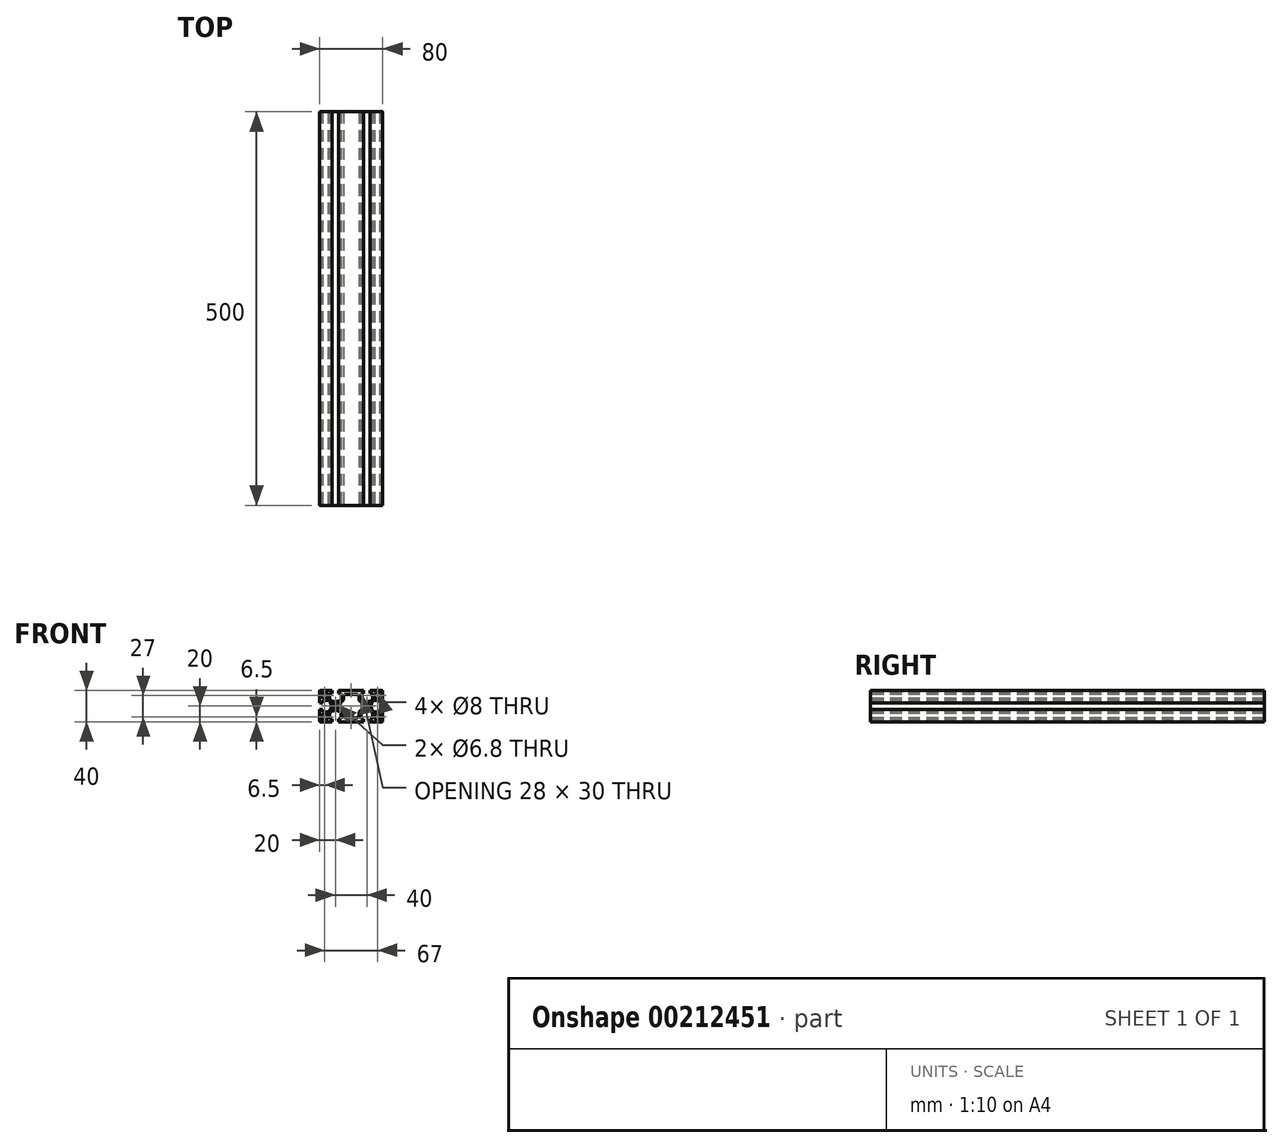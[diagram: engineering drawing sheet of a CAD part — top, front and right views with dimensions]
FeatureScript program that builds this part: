
annotation { "Feature Type Name" : "Feature", "Feature Type Description" : "" }
export const myFeature = defineFeature(function(context is Context, id is Id, definition is map)
    precondition{}
    {
        {
            assignVariable(context, id + "F0", {"name" : "L", "anyValue" : 500});
        }
        {
            var Q0;
            Q0=qCreatedBy(makeId("Front.planeOp"),FACE);
            var sketch = newSketch(context, id + "F1", { "sketchPlane" : qUnion([Q0])});
            skLineSegment(sketch, "E0.bottom", {"start": v(40, 20) * mm, "end": v(-40, 20) * mm});
            skLineSegment(sketch, "E0.top", {"start": v(40, -20) * mm, "end": v(-40, -20) * mm});
            skLineSegment(sketch, "E0.left", {"start": v(40, 20) * mm, "end": v(40, -20) * mm});
            skLineSegment(sketch, "E0.right", {"start": v(-40, 20) * mm, "end": v(-40, -20) * mm});
            skPoint(sketch, "E0.middle", {"position": v(0, 0) * mm});
            skSolve(sketch);
        }
        {
            var Q0;
            Q0=qSketchRegion(id+"F1",true);
            extrude(context, id + "F2", {"entities" : qUnion([Q0]), "endBound" : BoundingType.SYMMETRIC, "depth" : (getVariable(context, 'L')) * mm});
        }
        {
            var Q0;
            Q0=qCreatedBy(makeId("Front.planeOp"),FACE);
            var sketch = newSketch(context, id + "F3", { "sketchPlane" : qUnion([Q0])});
            skLineSegment(sketch, "E1.bottom", {"start": v(33.5, 13.5) * mm, "end": v(-33.5, 13.5) * mm, "construction": true});
            skLineSegment(sketch, "E1.top", {"start": v(33.5, -13.5) * mm, "end": v(-33.5, -13.5) * mm, "construction": true});
            skLineSegment(sketch, "E1.left", {"start": v(33.5, 13.5) * mm, "end": v(33.5, -13.5) * mm, "construction": true});
            skLineSegment(sketch, "E1.right", {"start": v(-33.5, 13.5) * mm, "end": v(-33.5, -13.5) * mm, "construction": true});
            skPoint(sketch, "E1.middle", {"position": v(0, 0) * mm});
            skCircle(sketch, "E2", {"center": v(-33.5, 13.5) * mm, "radius": 4 * mm});
            skCircle(sketch, "E3", {"center": v(-33.5, -13.5) * mm, "radius": 4 * mm});
            skCircle(sketch, "E4", {"center": v(33.5, -13.5) * mm, "radius": 4 * mm});
            skCircle(sketch, "E5", {"center": v(33.5, 13.5) * mm, "radius": 4 * mm});
            skLineSegment(sketch, "E6", {"start": v(-20, 0) * mm, "end": v(20, 0) * mm, "construction": true});
            skCircle(sketch, "E7", {"center": v(-20, 0) * mm, "radius": 3.4 * mm});
            skCircle(sketch, "E8", {"center": v(20, 0) * mm, "radius": 3.4 * mm});
            skSolve(sketch);
        }
        {
            var Q0;
            Q0=qSketchRegion(id+"F3",true);
            extrude(context, id + "F4", {"entities" : qUnion([Q0]), "operationType" : NewBodyOperationType.REMOVE, "endBound" : BoundingType.THROUGH_ALL, "oppositeDirection" : true, "depth" : 25 * mm, "hasSecondDirection" : true, "secondDirectionBound" : SecondDirectionBoundingType.THROUGH_ALL, "secondDirectionOppositeDirection" : false, "secondDirectionDepth" : 25 * mm});
        }
        {
            var Q0;
            Q0=qCreatedBy(makeId("Front.planeOp"),FACE);
            var sketch = newSketch(context, id + "F5", { "sketchPlane" : qUnion([Q0])});
            skLineSegment(sketch, "E9", {"start": v(-24.2, 20) * mm, "end": v(-15.8, 20) * mm});
            skLineSegment(sketch, "E10", {"start": v(-15.8, 20) * mm, "end": v(-15.8, 16) * mm});
            skLineSegment(sketch, "E11", {"start": v(-15.8, 16) * mm, "end": v(-12.75, 16) * mm});
            skLineSegment(sketch, "E12", {"start": v(-12.75, 16) * mm, "end": v(-12.75, 8.86) * mm});
            skLineSegment(sketch, "E13", {"start": v(-24.2, 20) * mm, "end": v(-24.2, 16) * mm});
            skLineSegment(sketch, "E14", {"start": v(-24.2, 16) * mm, "end": v(-27.25, 16) * mm});
            skLineSegment(sketch, "E15", {"start": v(-27.25, 16) * mm, "end": v(-27.25, 8.86) * mm});
            skLineSegment(sketch, "E16", {"start": v(-20, 20) * mm, "end": v(-20, 0) * mm, "construction": true});
            skArc(sketch, "E17", {"start": v(-27.25, 8.86) * mm, "mid": v(-20, 5.5) * mm, "end": v(-12.75, 8.86) * mm});
            skLineSegment(sketch, "E18.1.0", {"start": v(-40, -4.2) * mm, "end": v(-36, -4.2) * mm});
            skLineSegment(sketch, "E18.1.1", {"start": v(-36, -4.2) * mm, "end": v(-36, -7.25) * mm});
            skLineSegment(sketch, "E18.1.2", {"start": v(-36, -7.25) * mm, "end": v(-28.86, -7.25) * mm});
            skArc(sketch, "E18.1.3", {"start": v(-28.86, -7.25) * mm, "mid": v(-25.5, 0) * mm, "end": v(-28.86, 7.25) * mm});
            skLineSegment(sketch, "E18.1.4", {"start": v(-36, 7.25) * mm, "end": v(-28.86, 7.25) * mm});
            skLineSegment(sketch, "E18.1.5", {"start": v(-36, 4.2) * mm, "end": v(-36, 7.25) * mm});
            skLineSegment(sketch, "E18.1.6", {"start": v(-40, 4.2) * mm, "end": v(-36, 4.2) * mm});
            skLineSegment(sketch, "E18.1.7", {"start": v(-40, -4.2) * mm, "end": v(-40, 4.2) * mm});
            skLineSegment(sketch, "E18.2.0", {"start": v(-15.8, -20) * mm, "end": v(-15.8, -16) * mm});
            skLineSegment(sketch, "E18.2.1", {"start": v(-15.8, -16) * mm, "end": v(-12.75, -16) * mm});
            skLineSegment(sketch, "E18.2.2", {"start": v(-12.75, -16) * mm, "end": v(-12.75, -8.86) * mm});
            skArc(sketch, "E18.2.3", {"start": v(-12.75, -8.86) * mm, "mid": v(-20, -5.5) * mm, "end": v(-27.25, -8.86) * mm});
            skLineSegment(sketch, "E18.2.4", {"start": v(-27.25, -16) * mm, "end": v(-27.25, -8.86) * mm});
            skLineSegment(sketch, "E18.2.5", {"start": v(-24.2, -16) * mm, "end": v(-27.25, -16) * mm});
            skLineSegment(sketch, "E18.2.6", {"start": v(-24.2, -20) * mm, "end": v(-24.2, -16) * mm});
            skLineSegment(sketch, "E18.2.7", {"start": v(-15.8, -20) * mm, "end": v(-24.2, -20) * mm});
            skPoint(sketch, "E18.center", {"position": v(-20, 0) * mm});
            skLineSegment(sketch, "E18.anchor1", {"start": v(-20, 0) * mm, "end": v(-24.2, 16) * mm, "construction": true});
            skLineSegment(sketch, "E18.anchor2", {"start": v(-20, 0) * mm, "end": v(-15.8, -16) * mm, "construction": true});
            skLineSegment(sketch, "E19", {"start": v(0, -20) * mm, "end": v(0, 24.43) * mm, "construction": true});
            skArc(sketch, "E20.MirrorCS", {"start": v(12.75, -8.86) * mm, "mid": v(20, -5.5) * mm, "end": v(27.25, -8.86) * mm});
            skLineSegment(sketch, "E21.MirrorCS", {"start": v(40, -4.2) * mm, "end": v(36, -4.2) * mm});
            skLineSegment(sketch, "E22.MirrorCS", {"start": v(12.75, 16) * mm, "end": v(12.75, 8.86) * mm});
            skLineSegment(sketch, "E23.MirrorCS", {"start": v(27.25, -16) * mm, "end": v(27.25, -8.86) * mm});
            skLineSegment(sketch, "E24.MirrorCS", {"start": v(20, 0) * mm, "end": v(15.8, -16) * mm, "construction": true});
            skLineSegment(sketch, "E25.MirrorCS", {"start": v(15.8, -16) * mm, "end": v(12.75, -16) * mm});
            skPoint(sketch, "E26.MirrorP", {"position": v(20, 0) * mm});
            skLineSegment(sketch, "E27.MirrorCS", {"start": v(24.2, -16) * mm, "end": v(27.25, -16) * mm});
            skLineSegment(sketch, "E28.MirrorCS", {"start": v(20, 20) * mm, "end": v(20, 0) * mm, "construction": true});
            skLineSegment(sketch, "E29.MirrorCS", {"start": v(20, 0) * mm, "end": v(24.2, 16) * mm, "construction": true});
            skLineSegment(sketch, "E30.MirrorCS", {"start": v(40, -4.2) * mm, "end": v(40, 4.2) * mm});
            skArc(sketch, "E31.MirrorCS", {"start": v(28.86, -7.25) * mm, "mid": v(25.5, 0) * mm, "end": v(28.86, 7.25) * mm});
            skLineSegment(sketch, "E32.MirrorCS", {"start": v(36, -7.25) * mm, "end": v(28.86, -7.25) * mm});
            skLineSegment(sketch, "E33.MirrorCS", {"start": v(36, -4.2) * mm, "end": v(36, -7.25) * mm});
            skArc(sketch, "E34.MirrorCS", {"start": v(27.25, 8.86) * mm, "mid": v(20, 5.5) * mm, "end": v(12.75, 8.86) * mm});
            skLineSegment(sketch, "E35.MirrorCS", {"start": v(27.25, 16) * mm, "end": v(27.25, 8.86) * mm});
            skLineSegment(sketch, "E36.MirrorCS", {"start": v(15.8, -20) * mm, "end": v(24.2, -20) * mm});
            skLineSegment(sketch, "E37.MirrorCS", {"start": v(24.2, -20) * mm, "end": v(24.2, -16) * mm});
            skLineSegment(sketch, "E38.MirrorCS", {"start": v(24.2, 20) * mm, "end": v(24.2, 16) * mm});
            skLineSegment(sketch, "E39.MirrorCS", {"start": v(15.8, 16) * mm, "end": v(12.75, 16) * mm});
            skLineSegment(sketch, "E40.MirrorCS", {"start": v(15.8, 20) * mm, "end": v(15.8, 16) * mm});
            skLineSegment(sketch, "E41.MirrorCS", {"start": v(24.2, 20) * mm, "end": v(15.8, 20) * mm});
            skLineSegment(sketch, "E42.MirrorCS", {"start": v(15.8, -20) * mm, "end": v(15.8, -16) * mm});
            skLineSegment(sketch, "E43.MirrorCS", {"start": v(12.75, -16) * mm, "end": v(12.75, -8.86) * mm});
            skLineSegment(sketch, "E44.MirrorCS", {"start": v(40, 4.2) * mm, "end": v(36, 4.2) * mm});
            skLineSegment(sketch, "E45.MirrorCS", {"start": v(36, 7.25) * mm, "end": v(28.86, 7.25) * mm});
            skLineSegment(sketch, "E46.MirrorCS", {"start": v(36, 4.2) * mm, "end": v(36, 7.25) * mm});
            skLineSegment(sketch, "E47.MirrorCS", {"start": v(24.2, 16) * mm, "end": v(27.25, 16) * mm});
            skSolve(sketch);
        }
        {
            var Q0;
            Q0=qSketchRegion(id+"F5",true);
            extrude(context, id + "F6", {"entities" : qUnion([Q0]), "operationType" : NewBodyOperationType.REMOVE, "endBound" : BoundingType.THROUGH_ALL, "oppositeDirection" : true, "depth" : 25 * mm, "hasSecondDirection" : true, "secondDirectionBound" : SecondDirectionBoundingType.THROUGH_ALL, "secondDirectionOppositeDirection" : false, "secondDirectionDepth" : 25 * mm});
        }
        {
            var Q0;
            Q0=qCreatedBy(makeId("Front.planeOp"),FACE);
            var sketch = newSketch(context, id + "F7", { "sketchPlane" : qUnion([Q0])});
            skLineSegment(sketch, "E48.bottom", {"start": v(-6.75, 15) * mm, "end": v(6.75, 15) * mm});
            skLineSegment(sketch, "E48.top", {"start": v(-6.75, -15) * mm, "end": v(6.75, -15) * mm});
            skLineSegment(sketch, "E48.left", {"start": v(-9.75, 12) * mm, "end": v(-9.75, 7.85) * mm});
            skLineSegment(sketch, "E48.right", {"start": v(9.75, 12) * mm, "end": v(9.75, 7.85) * mm});
            skLineSegment(sketch, "E49.left", {"start": v(-14, 4.03) * mm, "end": v(-14, -4.03) * mm});
            skLineSegment(sketch, "E49.right", {"start": v(14, 4.03) * mm, "end": v(14, -4.03) * mm});
            skLineSegment(sketch, "E50", {"start": v(0, 15) * mm, "end": v(0, -15) * mm, "construction": true});
            skLineSegment(sketch, "E51", {"start": v(0, 20) * mm, "end": v(0, -26.61) * mm, "construction": true});
            skArc(sketch, "E52.0", {"start": v(-14, 4.03) * mm, "mid": v(-11.65, 5.7) * mm, "end": v(-9.75, 7.85) * mm});
            skLineSegment(sketch, "E53", {"start": v(-20, 0) * mm, "end": v(20, 0) * mm, "construction": true});
            skArc(sketch, "E54.0", {"start": v(-9.75, -7.85) * mm, "mid": v(-11.65, -5.7) * mm, "end": v(-14, -4.03) * mm});
            skArc(sketch, "E55.0", {"start": v(14, 4.03) * mm, "mid": v(11.65, 5.7) * mm, "end": v(9.75, 7.85) * mm});
            skArc(sketch, "E56.0", {"start": v(9.75, -7.85) * mm, "mid": v(11.65, -5.7) * mm, "end": v(14, -4.03) * mm});
            skLineSegment(sketch, "E57.trimOffspring", {"start": v(9.75, -7.85) * mm, "end": v(9.75, -12) * mm});
            skLineSegment(sketch, "E58.trimOffspring", {"start": v(-9.75, -7.85) * mm, "end": v(-9.75, -12) * mm});
            skPoint(sketch, "E59.visualSharp", {"position": v(-9.75, 15) * mm});
            skArc(sketch, "E59.filletArc", {"start": v(-6.75, 15) * mm, "mid": v(-8.87, 14.12) * mm, "end": v(-9.75, 12) * mm});
            skPoint(sketch, "E60.visualSharp", {"position": v(-9.75, -15) * mm});
            skArc(sketch, "E60.filletArc", {"start": v(-9.75, -12) * mm, "mid": v(-8.87, -14.12) * mm, "end": v(-6.75, -15) * mm});
            skPoint(sketch, "E61.visualSharp", {"position": v(9.75, -15) * mm});
            skArc(sketch, "E61.filletArc", {"start": v(6.75, -15) * mm, "mid": v(8.87, -14.12) * mm, "end": v(9.75, -12) * mm});
            skPoint(sketch, "E62.visualSharp", {"position": v(9.75, 15) * mm});
            skArc(sketch, "E62.filletArc", {"start": v(9.75, 12) * mm, "mid": v(8.87, 14.12) * mm, "end": v(6.75, 15) * mm});
            skSolve(sketch);
        }
        {
            var Q0;
            Q0=qSketchRegion(id+"F7",true);
            extrude(context, id + "F8", {"entities" : qUnion([Q0]), "operationType" : NewBodyOperationType.REMOVE, "endBound" : BoundingType.THROUGH_ALL, "oppositeDirection" : true, "depth" : 25 * mm, "hasSecondDirection" : true, "secondDirectionBound" : SecondDirectionBoundingType.THROUGH_ALL, "secondDirectionOppositeDirection" : false, "secondDirectionDepth" : 25 * mm});
        }
        {
            var Q0;
            Q0=makeQuery(id+"F2.opExtrude","SWEPT_EDGE",EDGE,{"disambiguationData":[OSD([sQuery(id+"F1.wireOp",EDGE,"E0.bottom"),sQuery(id+"F1.wireOp",EDGE,"E0.right")])]});
            var Q1;
            Q1=makeQuery(id+"F2.opExtrude","SWEPT_EDGE",EDGE,{"disambiguationData":[OSD([sQuery(id+"F1.wireOp",EDGE,"E0.bottom"),sQuery(id+"F1.wireOp",EDGE,"E0.left")])]});
            var Q2;
            Q2=makeQuery(id+"F2.opExtrude","SWEPT_EDGE",EDGE,{"disambiguationData":[OSD([sQuery(id+"F1.wireOp",EDGE,"E0.top"),sQuery(id+"F1.wireOp",EDGE,"E0.left")])]});
            var Q3;
            Q3=makeQuery(id+"F2.opExtrude","SWEPT_EDGE",EDGE,{"disambiguationData":[OSD([sQuery(id+"F1.wireOp",EDGE,"E0.top"),sQuery(id+"F1.wireOp",EDGE,"E0.right")])]});
            fillet(context, id + "F9", {"entities" : qUnion([Q0, Q1, Q2, Q3]), "radius" : 1 * mm, "tangentPropagation" : true, "allowEdgeOverflow" : false});
        }
    });
